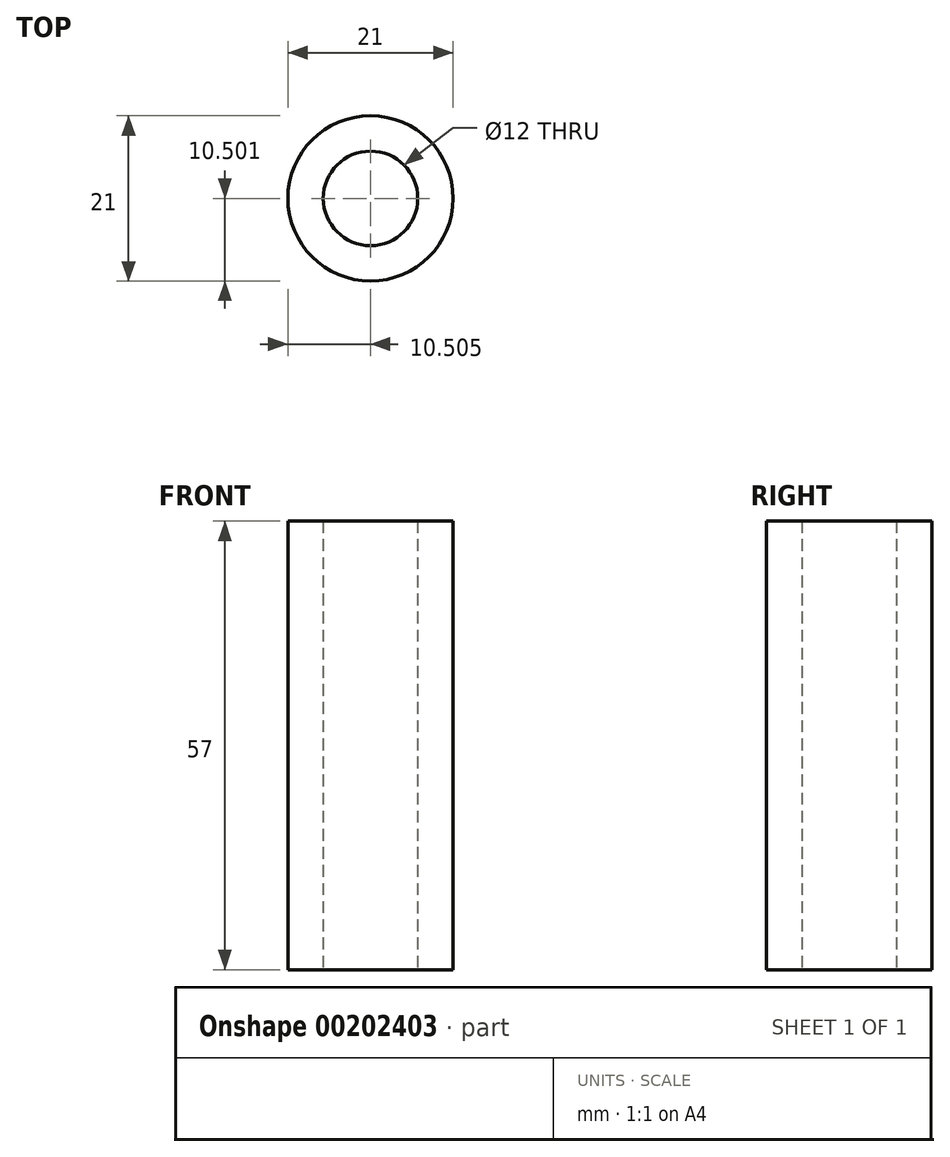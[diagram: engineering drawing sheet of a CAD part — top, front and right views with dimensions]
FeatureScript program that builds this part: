
annotation { "Feature Type Name" : "Feature", "Feature Type Description" : "" }
export const myFeature = defineFeature(function(context is Context, id is Id, definition is map)
    precondition{}
    {
        {
            var Q0;
            Q0=qCreatedBy(makeId("Top.planeOp"),FACE);
            var sketch = newSketch(context, id + "F0", { "sketchPlane" : qUnion([Q0])});
            skCircle(sketch, "E0", {"center": v(-60.37, -58.2) * mm, "radius": 6 * mm});
            skCircle(sketch, "E1", {"center": v(-60.37, -58.2) * mm, "radius": 10.5 * mm});
            skSolve(sketch);
        }
        {
            var Q0;
            Q0=makeQuery(id+"F0.imprint","IMPRINT",FACE,{"disambiguationData":[TD([[makeQuery(id+"F0.imprint","IMPRINT",EDGE,{"derivedFrom":sQuery(id+"F0.wireOp",EDGE,"E0")}),-1.0]])]});
            extrude(context, id + "F1", {"entities" : qUnion([Q0]), "depth" : 57 * mm});
        }
    });
